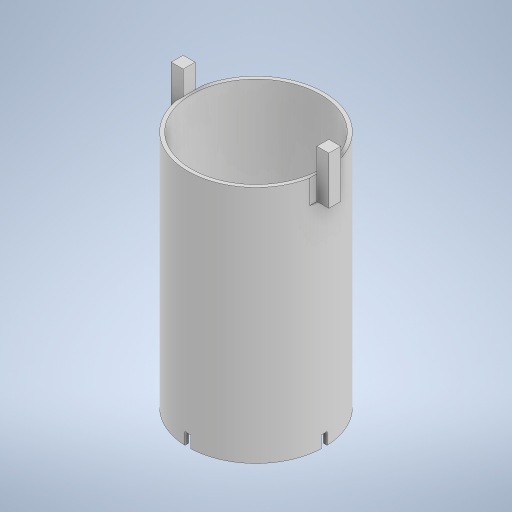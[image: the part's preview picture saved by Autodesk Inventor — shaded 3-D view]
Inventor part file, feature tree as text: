
AUTODESK INVENTOR PART (.ipt)
format: ipt  version: 2024.3 (Build 283343000, 343)  size: 273,920 bytes
history: native  units: mm
features: extrude x4, sketch x4, mirror x1
ambient origin geometry x8: Origin, YZ Plane, XZ Plane, XY Plane, X Axis, Y Axis, Z Axis, Center Point
bodies: Solid1 (feature_tree)
feature tree (9):
  extrude  "Extrusion1"  Depth=114.0mm
  extrude  "Extrusion2"  Depth=200.0mm
  extrude  "Extrusion3"  Depth=40.0mm
  mirror  "Mirror1"
  extrude  "Extrusion4"  Depth=10.0mm
  sketch  "Sketch1"  dims[d0=3.0mm d1=114.0mm]
  sketch  "Sketch2"  dims[d2=200.0mm d3=0.0mm d4=22.0mm]
  sketch  "Sketch3"  dims[d5=20.0mm d6=0.0mm d7=40.0mm]
  sketch  "Sketch4"  dims[d8=10.0mm d9=6.0mm d10=10.0mm d11=0.0mm d12=5.0mm d13=5.0mm d14=120.0mm d15=120.0mm d16=10.0mm d17=0.0mm]
